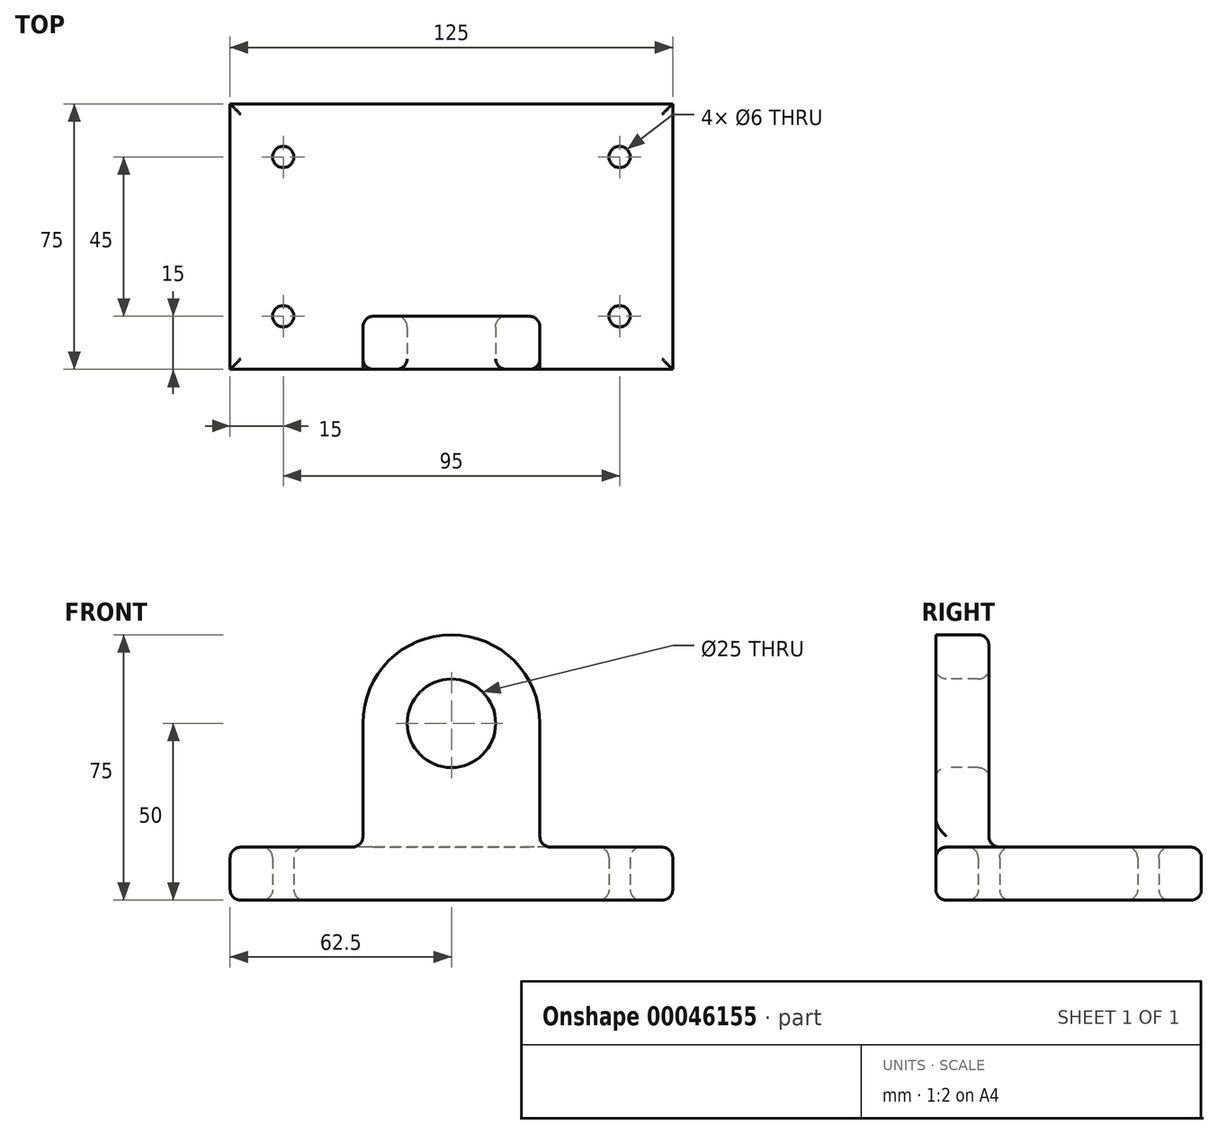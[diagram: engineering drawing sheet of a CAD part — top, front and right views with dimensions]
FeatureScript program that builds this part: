
annotation { "Feature Type Name" : "Feature", "Feature Type Description" : "" }
export const myFeature = defineFeature(function(context is Context, id is Id, definition is map)
    precondition{}
    {
        {
            var Q0;
            Q0=qCreatedBy(makeId("Top.planeOp"),FACE);
            var sketch = newSketch(context, id + "F0", { "sketchPlane" : qUnion([Q0])});
            skLineSegment(sketch, "E0.rect.bottom", {"start": v(62.5, 37.5) * mm, "end": v(-62.5, 37.5) * mm});
            skLineSegment(sketch, "E0.rect.top", {"start": v(62.5, -37.5) * mm, "end": v(-62.5, -37.5) * mm});
            skLineSegment(sketch, "E0.rect.left", {"start": v(62.5, 37.5) * mm, "end": v(62.5, -37.5) * mm});
            skLineSegment(sketch, "E0.rect.right", {"start": v(-62.5, 37.5) * mm, "end": v(-62.5, -37.5) * mm});
            skPoint(sketch, "E0.rect.middle", {"position": v(0, 0) * mm});
            skLineSegment(sketch, "E1.rect.bottom", {"start": v(47.5, 22.5) * mm, "end": v(-47.5, 22.5) * mm, "construction": true});
            skLineSegment(sketch, "E1.rect.top", {"start": v(47.5, -22.5) * mm, "end": v(-47.5, -22.5) * mm, "construction": true});
            skLineSegment(sketch, "E1.rect.left", {"start": v(47.5, 22.5) * mm, "end": v(47.5, -22.5) * mm, "construction": true});
            skLineSegment(sketch, "E1.rect.right", {"start": v(-47.5, 22.5) * mm, "end": v(-47.5, -22.5) * mm, "construction": true});
            skCircle(sketch, "E2", {"center": v(-47.5, 22.5) * mm, "radius": 3 * mm});
            skCircle(sketch, "E3", {"center": v(47.5, 22.5) * mm, "radius": 3 * mm});
            skCircle(sketch, "E4", {"center": v(47.5, -22.5) * mm, "radius": 3 * mm});
            skCircle(sketch, "E5", {"center": v(-47.5, -22.5) * mm, "radius": 3 * mm});
            skSolve(sketch);
        }
        {
            var Q0;
            Q0=makeQuery(id+"F0.imprint","IMPRINT",FACE,{"disambiguationData":[TD([[makeQuery(id+"F0.imprint","IMPRINT",EDGE,{"derivedFrom":sQuery(id+"F0.wireOp",EDGE,"E0.rect.bottom")}),1.0]])]});
            extrude(context, id + "F1", {"entities" : qUnion([Q0]), "depth" : 15 * mm});
        }
        {
            var Q0;
            Q0=makeQuery(id+"F1.opExtrude","SWEPT_FACE",FACE,{"disambiguationData":[OSD([sQuery(id+"F0.wireOp",EDGE,"E0.rect.top")])]});
            var sketch = newSketch(context, id + "F2", { "sketchPlane" : qUnion([Q0])});
            skLineSegment(sketch, "E6", {"start": v(0, 0) * mm, "end": v(0, 50) * mm, "construction": true});
            skCircle(sketch, "E7", {"center": v(0, 50) * mm, "radius": 25 * mm});
            skLineSegment(sketch, "E8.bottom", {"start": v(-25, 50) * mm, "end": v(25, 50) * mm});
            skLineSegment(sketch, "E8.top", {"start": v(-25, 0) * mm, "end": v(25, 0) * mm});
            skLineSegment(sketch, "E8.left", {"start": v(-25, 50) * mm, "end": v(-25, 0) * mm});
            skLineSegment(sketch, "E8.right", {"start": v(25, 50) * mm, "end": v(25, 0) * mm});
            skCircle(sketch, "E9", {"center": v(0, 50) * mm, "radius": 12.5 * mm});
            skSolve(sketch);
        }
        {
            var Q0;
            {var subQ0=sQuery(id+"F2.wireOp",EDGE,"E8.bottom");Q0=makeQuery(id+"F2.imprint","IMPRINT",FACE,{"disambiguationData":[TD([[makeQuery(id+"F2.imprint","IMPRINT",EDGE,{"derivedFrom":subQ0}),1.0]])]});}
            var Q1;
            {var subQ0=sQuery(id+"F2.wireOp",EDGE,"E8.bottom");Q1=makeQuery(id+"F2.imprint","IMPRINT",FACE,{"disambiguationData":[TD([[makeQuery(id+"F2.imprint","IMPRINT",EDGE,{"derivedFrom":subQ0}),-1.0]])]});}
            var Q2;
            {var subQ0=makeQuery(id+"F1.opExtrude","CAP_EDGE",EDGE,{"disambiguationData":[OSD([sQuery(id+"F0.wireOp",EDGE,"E0.rect.top")])],"isStart":false});var subQ3=sQuery(id+"F2.wireOp",EDGE,"E8.left");var subQ4=makeQuery(id+"F2.imprint","INTERSECT",VERTEX,{"derivedFrom":[subQ0,subQ3]});Q2=makeQuery(id+"F2.imprint","IMPRINT",FACE,{"disambiguationData":[TD([[makeQuery(id+"F2.imprint","IMPRINT",EDGE,{"disambiguationData":[TD([[subQ4,1.0]])],"derivedFrom":subQ0}),-1.0]])]});}
            var Q3;
            {var subQ7=sQuery(id+"F2.wireOp",EDGE,"E8.top");Q3=makeQuery(id+"F2.imprint","IMPRINT",FACE,{"disambiguationData":[TD([[makeQuery(id+"F2.imprint","IMPRINT",EDGE,{"derivedFrom":subQ7}),-1.0]])]});}
            extrude(context, id + "F3", {"entities" : qUnion([Q0, Q1, Q2, Q3]), "operationType" : NewBodyOperationType.ADD, "oppositeDirection" : true, "depth" : 15 * mm});
        }
        {
            var Q0;
            Q0=makeQuery(id+"F1.opExtrude","CAP_FACE",FACE,{"disambiguationData":[OSD([sQuery(id+"F0.wireOp",EDGE,"E0.rect.bottom"),sQuery(id+"F0.wireOp",EDGE,"E0.rect.top"),sQuery(id+"F0.wireOp",EDGE,"E0.rect.left"),sQuery(id+"F0.wireOp",EDGE,"E0.rect.right"),sQuery(id+"F0.wireOp",EDGE,"E2"),sQuery(id+"F0.wireOp",EDGE,"E3"),sQuery(id+"F0.wireOp",EDGE,"E4"),sQuery(id+"F0.wireOp",EDGE,"E5")])],"isStart":false});
            var Q1;
            Q1=makeQuery(id+"F3.opExtrude","CAP_FACE",FACE,{"disambiguationData":[OSD([sQuery(id+"F2.wireOp",EDGE,"E7"),sQuery(id+"F2.wireOp",EDGE,"E8.top"),sQuery(id+"F2.wireOp",EDGE,"E8.left"),sQuery(id+"F2.wireOp",EDGE,"E8.right"),sQuery(id+"F2.wireOp",EDGE,"E9")])],"isStart":false});
            var Q2;
            Q2=makeQuery(id+"F3.opExtrude","CAP_EDGE",EDGE,{"disambiguationData":[OSD([sQuery(id+"F2.wireOp",EDGE,"E9")])],"isStart":true});
            var Q3;
            Q3=makeQuery(id+"F1.opExtrude","CAP_FACE",FACE,{"disambiguationData":[OSD([sQuery(id+"F0.wireOp",EDGE,"E0.rect.bottom"),sQuery(id+"F0.wireOp",EDGE,"E0.rect.top"),sQuery(id+"F0.wireOp",EDGE,"E0.rect.left"),sQuery(id+"F0.wireOp",EDGE,"E0.rect.right"),sQuery(id+"F0.wireOp",EDGE,"E2"),sQuery(id+"F0.wireOp",EDGE,"E3"),sQuery(id+"F0.wireOp",EDGE,"E4"),sQuery(id+"F0.wireOp",EDGE,"E5")])],"isStart":true});
            fillet(context, id + "F4", {"entities" : qUnion([Q0, Q1, Q2, Q3]), "radius" : 3 * mm, "tangentPropagation" : true, "allowEdgeOverflow" : false});
        }
    });
